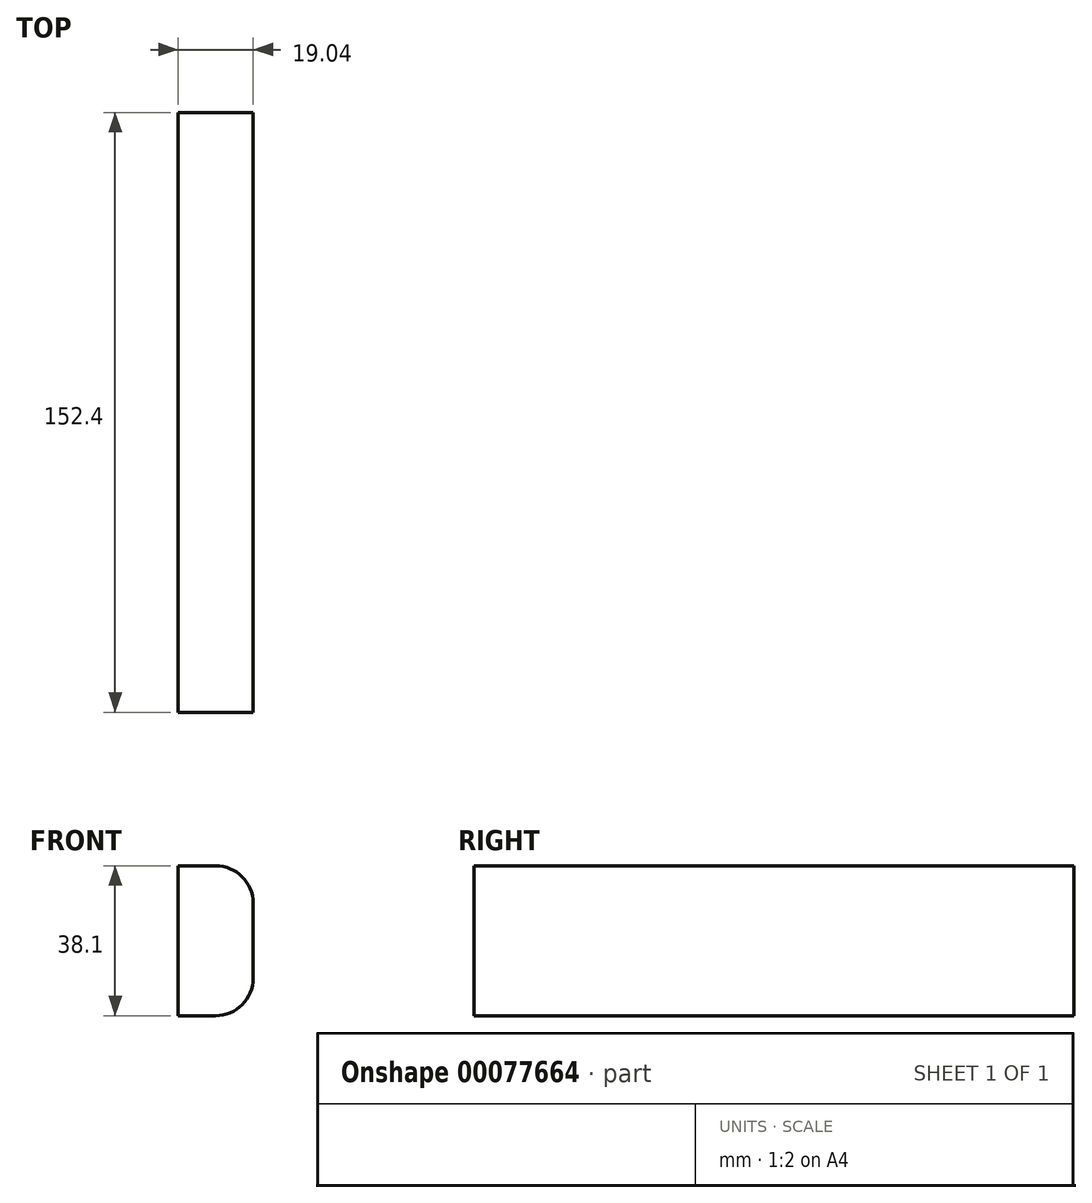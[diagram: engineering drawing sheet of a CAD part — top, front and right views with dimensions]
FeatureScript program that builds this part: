
annotation { "Feature Type Name" : "Feature", "Feature Type Description" : "" }
export const myFeature = defineFeature(function(context is Context, id is Id, definition is map)
    precondition{}
    {
        {
            var Q0;
            Q0=qCreatedBy(makeId("Front.planeOp"),FACE);
            var sketch = newSketch(context, id + "F0", { "sketchPlane" : qUnion([Q0])});
            skLineSegment(sketch, "E0", {"start": v(-9.52, -19.05) * mm, "end": v(-9.52, 19.05) * mm});
            skLineSegment(sketch, "E1", {"start": v(0, -19.05) * mm, "end": v(-9.52, -19.05) * mm});
            skLineSegment(sketch, "E2", {"start": v(9.52, 9.52) * mm, "end": v(9.52, -9.52) * mm});
            skLineSegment(sketch, "E3", {"start": v(-9.52, 19.05) * mm, "end": v(0, 19.05) * mm});
            skArc(sketch, "E4", {"start": v(9.52, 9.52) * mm, "mid": v(6.74, 16.26) * mm, "end": v(0, 19.05) * mm});
            skArc(sketch, "E5", {"start": v(0, -19.05) * mm, "mid": v(6.74, -16.26) * mm, "end": v(9.52, -9.52) * mm});
            skSolve(sketch);
        }
        {
            var Q0;
            Q0=makeQuery(id+"F0.imprint","IMPRINT",FACE,{"disambiguationData":[TD([[makeQuery(id+"F0.imprint","IMPRINT",EDGE,{"derivedFrom":sQuery(id+"F0.wireOp",EDGE,"E0")}),-1.0]])]});
            extrude(context, id + "F1", {"entities" : qUnion([Q0]), "depth" : 152.4 * mm});
        }
    });
